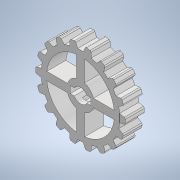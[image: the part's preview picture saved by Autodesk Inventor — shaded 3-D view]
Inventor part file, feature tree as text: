
AUTODESK INVENTOR PART (.ipt)
format: ipt  version: 2022 (Build 260153000, 153)  size: 396,288 bytes
history: native  units: mm
features: extrude x4, sketch x4, other x4, reference x2, plane x1, projected_geometry x1
ambient origin geometry x8: Origin, YZ Plane, XZ Plane, XY Plane, X Axis, Y Axis, Z Axis, Center Point
bodies: Solid1 (feature_tree)
feature tree (16):
  extrude  "Extrusion1"  Depth=10.0mm
  sketch  "Sketch2"  dims[d2=2.0mm d3=5.0mm d4=0.0mm d5=0.0mm d6=40.0mm d8=360.0deg]
  plane  "Work Plane1"
  extrude  "Extrusion2"  Depth=5.0mm TaperAngle=360.0deg
  extrude  "Extrusion3"  TaperAngle=0.0deg  [1 undecoded]
  extrude  "Extrusion4"  Depth=10.0mm
  sketch  "Sketch1"  dims[d0=10.0mm d1=0.3mm]
  reference  "Reference1"
  projected_geometry  "Projected Loop1"
  sketch  "Sketch3"  dims[d10=2.0mm d11=0.0mm d12=0.0mm d13=0.0mm]
  sketch  "Sketch4"  dims[d14=33.0mm d15=33.0mm d16=2.0mm d17=2.0mm d18=3.0mm d19=40.0mm d21=360.0deg d23=2.0mm d24=3.0mm d25=0.5mm d26=0.5mm d27=180.0mm d29=360.0deg d31=10.0mm d32=0.0mm]
  reference  "Reference2"
  other  "<userpath>\OneDrive - Imperial College London\ROBOICP\new vial holder assembly.iam"
  other  "new vial holder assembly.iam"
  other  "Mixer:1"
  other  "mixer_gear:5"
note: 1 required parameter value undecoded (feature->parameter linkage not recoverable at this tier; creation-order binding heuristic only, values carry confidence <= 0.55)
